# Revit family: SAL 50
name_source: partatom
category: Air Terminals
revit_build: Autodesk Revit 2017 (Build: 20160225_1515(x64)
units: mm (PartAtom-declared; Revit-internal decimal feet)

## family parameters
Always vertical = Yes
Cut with Voids When Loaded = No
Part Type = Normal
Room Calculation Point = No
Round Connector Dimension = Use Diameter
Shared = No
Work Plane-Based = No

## types (40) — shared parameters
Lw dB(A) = 30/35/40
Max Flow = 0.0 L/s
Maß A = 58.5 mm  [stored 0.191929 ft]
Maß C = 75 mm
Min Flow = 0.0 L/s
Product material = RAL 9016

## per-type parameters (varying)
- 600_1-reihig mit Anschlusskasten: Gewicht (g/m)=5607; Index=1; Index L=1; Index Reihig=1; L=600 mm; Maß B=101 mm  [stored 0.331365 ft]; Maß E=38.4 mm  [stored 0.125984 ft]; Maß F=48 mm  [stored 0.15748 ft]; Maß H=277 mm  [stored 0.908793 ft]; Maß K=51 mm; Maß M=75 mm; Maß Ø D=158 mm; Maß Ø D1=156 mm; Mindest-abstand (m)=8.3/>15.0/>15.0; Stutzen (Stk.)=1; Visible 1 Reihig=Yes; Visible 1 Stutzen=Yes; Visible 2 Reihig=No; Visible 2 Stutzen=No; Visible 3 Reihig=No; Visible 4 Reihig=No; x krit (m)=8.4/10.6/13.8; y (m)=1.6/2.1/2.6; Δp (Pa) 1=18/25/38; Δp (Pa) 2=21/31/42
- 750_1-reihig mit Anschlusskasten: Gewicht (g/m)=5607; Index=1; Index L=2; Index Reihig=1; L=750 mm  [stored 2.46063 ft]; Maß B=101 mm  [stored 0.331365 ft]; Maß E=38.4 mm  [stored 0.125984 ft]; Maß F=48 mm  [stored 0.15748 ft]; Maß H=277 mm  [stored 0.908793 ft]; Maß K=51 mm; Maß M=75 mm; Maß Ø D=158 mm; Maß Ø D1=156 mm; Mindest-abstand (m)=8.3/>15.0/>15.0; Stutzen (Stk.)=1; Visible 1 Reihig=Yes; Visible 1 Stutzen=Yes; Visible 2 Reihig=No; Visible 2 Stutzen=No; Visible 3 Reihig=No; Visible 4 Reihig=No; x krit (m)=8.4/10.6/13.8; y (m)=1.6/2.1/2.6; Δp (Pa) 1=18/25/38; Δp (Pa) 2=21/31/42
- 900_1-reihig mit Anschlusskasten: Gewicht (g/m)=5607; Index=1; Index L=3; Index Reihig=1; L=900 mm  [stored 2.95276 ft]; Maß B=101 mm  [stored 0.331365 ft]; Maß E=38.4 mm  [stored 0.125984 ft]; Maß F=48 mm  [stored 0.15748 ft]; Maß H=277 mm  [stored 0.908793 ft]; Maß K=51 mm; Maß M=75 mm; Maß Ø D=158 mm; Maß Ø D1=156 mm; Mindest-abstand (m)=8.3/>15.0/>15.0; Stutzen (Stk.)=1; Visible 1 Reihig=Yes; Visible 1 Stutzen=Yes; Visible 2 Reihig=No; Visible 2 Stutzen=No; Visible 3 Reihig=No; Visible 4 Reihig=No; x krit (m)=8.4/10.6/13.8; y (m)=1.6/2.1/2.6; Δp (Pa) 1=18/25/38; Δp (Pa) 2=21/31/42
- 1050_1-reihig mit Anschlusskasten: Gewicht (g/m)=5607; Index=1; Index L=4; Index Reihig=1; L=1050 mm; Maß B=101 mm  [stored 0.331365 ft]; Maß E=38.4 mm  [stored 0.125984 ft]; Maß F=48 mm  [stored 0.15748 ft]; Maß H=277 mm  [stored 0.908793 ft]; Maß K=51 mm; Maß M=75 mm; Maß Ø D=158 mm; Maß Ø D1=156 mm; Mindest-abstand (m)=8.3/>15.0/>15.0; Stutzen (Stk.)=1; Visible 1 Reihig=Yes; Visible 1 Stutzen=Yes; Visible 2 Reihig=No; Visible 2 Stutzen=No; Visible 3 Reihig=No; Visible 4 Reihig=No; x krit (m)=8.4/10.6/13.8; y (m)=1.6/2.1/2.6; Δp (Pa) 1=18/25/38; Δp (Pa) 2=21/31/42
- 1200_1-reihig mit Anschlusskasten: Gewicht (g/m)=5607; Index=1; Index L=5; Index Reihig=1; L=1200 mm; Maß B=101 mm  [stored 0.331365 ft]; Maß E=38.4 mm  [stored 0.125984 ft]; Maß F=48 mm  [stored 0.15748 ft]; Maß H=277 mm  [stored 0.908793 ft]; Maß K=51 mm; Maß M=75 mm; Maß Ø D=158 mm; Maß Ø D1=156 mm; Mindest-abstand (m)=8.3/>15.0/>15.0; Stutzen (Stk.)=1; Visible 1 Reihig=Yes; Visible 1 Stutzen=Yes; Visible 2 Reihig=No; Visible 2 Stutzen=No; Visible 3 Reihig=No; Visible 4 Reihig=No; x krit (m)=8.4/10.6/13.8; y (m)=1.6/2.1/2.6; Δp (Pa) 1=18/25/38; Δp (Pa) 2=21/31/42
- 1350_1-reihig mit Anschlusskasten: Gewicht (g/m)=5607; Index=1; Index L=6; Index Reihig=1; L=1350 mm  [stored 4.42913 ft]; Maß B=101 mm  [stored 0.331365 ft]; Maß E=38.4 mm  [stored 0.125984 ft]; Maß F=48 mm  [stored 0.15748 ft]; Maß H=277 mm  [stored 0.908793 ft]; Maß K=51 mm; Maß M=75 mm; Maß Ø D=158 mm; Maß Ø D1=156 mm; Mindest-abstand (m)=8.3/>15.0/>15.0; Stutzen (Stk.)=1; Visible 1 Reihig=Yes; Visible 1 Stutzen=Yes; Visible 2 Reihig=No; Visible 2 Stutzen=No; Visible 3 Reihig=No; Visible 4 Reihig=No; x krit (m)=8.4/10.6/13.8; y (m)=1.6/2.1/2.6; Δp (Pa) 1=18/25/38; Δp (Pa) 2=21/31/42
- 1500_1-reihig mit Anschlusskasten: Gewicht (g/m)=5607; Index=1; Index L=7; Index Reihig=1; L=1500 mm  [stored 4.92126 ft]; Maß B=101 mm  [stored 0.331365 ft]; Maß E=38.4 mm  [stored 0.125984 ft]; Maß F=48 mm  [stored 0.15748 ft]; Maß H=277 mm  [stored 0.908793 ft]; Maß K=51 mm; Maß M=75 mm; Maß Ø D=158 mm; Maß Ø D1=156 mm; Mindest-abstand (m)=8.3/>15.0/>15.0; Stutzen (Stk.)=1; Visible 1 Reihig=Yes; Visible 1 Stutzen=Yes; Visible 2 Reihig=No; Visible 2 Stutzen=No; Visible 3 Reihig=No; Visible 4 Reihig=No; x krit (m)=8.4/10.6/13.8; y (m)=1.6/2.1/2.6; Δp (Pa) 1=18/25/38; Δp (Pa) 2=21/31/42
- 1650_1-reihig mit Anschlusskasten: Gewicht (g/m)=5607; Index=2; Index L=8; Index Reihig=1; L=1650 mm; Maß B=101 mm  [stored 0.331365 ft]; Maß E=38.4 mm  [stored 0.125984 ft]; Maß F=48 mm  [stored 0.15748 ft]; Maß H=277 mm  [stored 0.908793 ft]; Maß K=51 mm; Maß M=75 mm; Maß Ø D=158 mm; Maß Ø D1=156 mm; Mindest-abstand (m)=8.3/>15.0/>15.0; Stutzen (Stk.)=2; Visible 1 Reihig=Yes; Visible 1 Stutzen=No; Visible 2 Reihig=No; Visible 2 Stutzen=Yes; Visible 3 Reihig=No; Visible 4 Reihig=No; x krit (m)=8.4/10.6/13.8; y (m)=1.6/2.1/2.6; Δp (Pa) 1=18/25/38; Δp (Pa) 2=21/31/42
- 1800_1-reihig mit Anschlusskasten: Gewicht (g/m)=5607; Index=2; Index L=9; Index Reihig=1; L=1800 mm; Maß B=101 mm  [stored 0.331365 ft]; Maß E=38.4 mm  [stored 0.125984 ft]; Maß F=48 mm  [stored 0.15748 ft]; Maß H=277 mm  [stored 0.908793 ft]; Maß K=51 mm; Maß M=75 mm; Maß Ø D=158 mm; Maß Ø D1=156 mm; Mindest-abstand (m)=8.3/>15.0/>15.0; Stutzen (Stk.)=2; Visible 1 Reihig=Yes; Visible 1 Stutzen=No; Visible 2 Reihig=No; Visible 2 Stutzen=Yes; Visible 3 Reihig=No; Visible 4 Reihig=No; x krit (m)=8.4/10.6/13.8; y (m)=1.6/2.1/2.6; Δp (Pa) 1=18/25/38; Δp (Pa) 2=21/31/42
- 1950_1-reihig mit Anschlusskasten: Gewicht (g/m)=5607; Index=2; Index L=10; Index Reihig=1; L=1950 mm; Maß B=101 mm  [stored 0.331365 ft]; Maß E=38.4 mm  [stored 0.125984 ft]; Maß F=48 mm  [stored 0.15748 ft]; Maß H=277 mm  [stored 0.908793 ft]; Maß K=51 mm; Maß M=75 mm; Maß Ø D=158 mm; Maß Ø D1=156 mm; Mindest-abstand (m)=8.3/>15.0/>15.0; Stutzen (Stk.)=2; Visible 1 Reihig=Yes; Visible 1 Stutzen=No; Visible 2 Reihig=No; Visible 2 Stutzen=Yes; Visible 3 Reihig=No; Visible 4 Reihig=No; x krit (m)=8.4/10.6/13.8; y (m)=1.6/2.1/2.6; Δp (Pa) 1=18/25/38; Δp (Pa) 2=21/31/42
- 600_2-reihig mit Anschlusskasten: Gewicht (g/m)=8293; Index=1; Index L=1; Index Reihig=2; L=600 mm; Maß B=148 mm  [stored 0.485564 ft]; Maß E=85 mm  [stored 0.278871 ft]; Maß F=94 mm  [stored 0.308399 ft]; Maß H=317 mm  [stored 1.04003 ft]; Maß K=97 mm  [stored 0.318241 ft]; Maß M=121 mm  [stored 0.396982 ft]; Maß Ø D=198 mm  [stored 0.649606 ft]; Maß Ø D1=196 mm  [stored 0.643045 ft]; Mindest-abstand (m)=15.0/>15.0/>15.0; Stutzen (Stk.)=1; Visible 1 Reihig=No; Visible 1 Stutzen=Yes; Visible 2 Reihig=Yes; Visible 2 Stutzen=No; Visible 3 Reihig=No; Visible 4 Reihig=No; x krit (m)=11.6/14.8/>15.0; y (m)=2.3/2.8/3.6; Δp (Pa) 1=15/22/30; Δp (Pa) 2=18/25/36
- 600_3-reihig mit Anschlusskasten: Gewicht (g/m)=10549; Index=1; Index L=1; Index Reihig=3; L=600 mm; Maß B=194 mm  [stored 0.636483 ft]; Maß E=131.6 mm  [stored 0.431759 ft]; Maß F=141 mm; Maß H=341 mm; Maß K=144 mm  [stored 0.472441 ft]; Maß M=168 mm  [stored 0.551181 ft]; Maß Ø D=222 mm; Maß Ø D1=220 mm  [stored 0.721785 ft]; Mindest-abstand (m)=15.0/>15.0/>15.0; Stutzen (Stk.)=1; Visible 1 Reihig=No; Visible 1 Stutzen=Yes; Visible 2 Reihig=No; Visible 2 Stutzen=No; Visible 3 Reihig=Yes; Visible 4 Reihig=No; x krit (m)=13.6/>15.0/>15.0; y (m)=2.7/3.4/4.3; Δp (Pa) 1=13/19/27; Δp (Pa) 2=16/22/31
- 600_4-reihig mit Anschlusskasten: Gewicht (g/m)=13135; Index=1; Index L=1; Index Reihig=4; L=600 mm; Maß B=241 mm  [stored 0.790682 ft]; Maß E=178.2 mm  [stored 0.584646 ft]; Maß F=187 mm  [stored 0.613517 ft]; Maß H=367 mm  [stored 1.20407 ft]; Maß K=190 mm; Maß M=215 mm; Maß Ø D=248 mm  [stored 0.813648 ft]; Maß Ø D1=246 mm  [stored 0.807087 ft]; Mindest-abstand (m)=15.0/>15.0/>15.0; Stutzen (Stk.)=1; Visible 1 Reihig=No; Visible 1 Stutzen=Yes; Visible 2 Reihig=No; Visible 2 Stutzen=No; Visible 3 Reihig=No; Visible 4 Reihig=Yes; x krit (m)=15.0/>15.0/>15.0; y (m)=3.0/3.8/4.7; Δp (Pa) 1=11/17/24; Δp (Pa) 2=14/20/28
- 750_2-reihig mit Anschlusskasten: Gewicht (g/m)=8293; Index=1; Index L=2; Index Reihig=2; L=750 mm  [stored 2.46063 ft]; Maß B=148 mm  [stored 0.485564 ft]; Maß E=85 mm  [stored 0.278871 ft]; Maß F=94 mm  [stored 0.308399 ft]; Maß H=317 mm  [stored 1.04003 ft]; Maß K=97 mm  [stored 0.318241 ft]; Maß M=121 mm  [stored 0.396982 ft]; Maß Ø D=198 mm  [stored 0.649606 ft]; Maß Ø D1=196 mm  [stored 0.643045 ft]; Mindest-abstand (m)=15.0/>15.0/>15.0; Stutzen (Stk.)=1; Visible 1 Reihig=No; Visible 1 Stutzen=Yes; Visible 2 Reihig=Yes; Visible 2 Stutzen=No; Visible 3 Reihig=No; Visible 4 Reihig=No; x krit (m)=11.6/14.8/>15.0; y (m)=2.3/2.8/3.6; Δp (Pa) 1=15/22/30; Δp (Pa) 2=18/25/36
- 750_3-reihig mit Anschlusskasten: Gewicht (g/m)=10549; Index=1; Index L=2; Index Reihig=3; L=750 mm  [stored 2.46063 ft]; Maß B=194 mm  [stored 0.636483 ft]; Maß E=131.6 mm  [stored 0.431759 ft]; Maß F=141 mm; Maß H=341 mm; Maß K=144 mm  [stored 0.472441 ft]; Maß M=168 mm  [stored 0.551181 ft]; Maß Ø D=222 mm; Maß Ø D1=220 mm  [stored 0.721785 ft]; Mindest-abstand (m)=15.0/>15.0/>15.0; Stutzen (Stk.)=1; Visible 1 Reihig=No; Visible 1 Stutzen=Yes; Visible 2 Reihig=No; Visible 2 Stutzen=No; Visible 3 Reihig=Yes; Visible 4 Reihig=No; x krit (m)=13.6/>15.0/>15.0; y (m)=2.7/3.4/4.3; Δp (Pa) 1=13/19/27; Δp (Pa) 2=16/22/31
- 750_4-reihig mit Anschlusskasten: Gewicht (g/m)=13135; Index=1; Index L=2; Index Reihig=4; L=750 mm  [stored 2.46063 ft]; Maß B=241 mm  [stored 0.790682 ft]; Maß E=178.2 mm  [stored 0.584646 ft]; Maß F=187 mm  [stored 0.613517 ft]; Maß H=367 mm  [stored 1.20407 ft]; Maß K=190 mm; Maß M=215 mm; Maß Ø D=248 mm  [stored 0.813648 ft]; Maß Ø D1=246 mm  [stored 0.807087 ft]; Mindest-abstand (m)=15.0/>15.0/>15.0; Stutzen (Stk.)=1; Visible 1 Reihig=No; Visible 1 Stutzen=Yes; Visible 2 Reihig=No; Visible 2 Stutzen=No; Visible 3 Reihig=No; Visible 4 Reihig=Yes; x krit (m)=15.0/>15.0/>15.0; y (m)=3.0/3.8/4.7; Δp (Pa) 1=11/17/24; Δp (Pa) 2=14/20/28
- 900_2-reihig mit Anschlusskasten: Gewicht (g/m)=8293; Index=1; Index L=3; Index Reihig=2; L=900 mm  [stored 2.95276 ft]; Maß B=148 mm  [stored 0.485564 ft]; Maß E=85 mm  [stored 0.278871 ft]; Maß F=94 mm  [stored 0.308399 ft]; Maß H=317 mm  [stored 1.04003 ft]; Maß K=97 mm  [stored 0.318241 ft]; Maß M=121 mm  [stored 0.396982 ft]; Maß Ø D=198 mm  [stored 0.649606 ft]; Maß Ø D1=196 mm  [stored 0.643045 ft]; Mindest-abstand (m)=15.0/>15.0/>15.0; Stutzen (Stk.)=1; Visible 1 Reihig=No; Visible 1 Stutzen=Yes; Visible 2 Reihig=Yes; Visible 2 Stutzen=No; Visible 3 Reihig=No; Visible 4 Reihig=No; x krit (m)=11.6/14.8/>15.0; y (m)=2.3/2.8/3.6; Δp (Pa) 1=15/22/30; Δp (Pa) 2=18/25/36
- 900_3-reihig mit Anschlusskasten: Gewicht (g/m)=10549; Index=1; Index L=3; Index Reihig=3; L=900 mm  [stored 2.95276 ft]; Maß B=194 mm  [stored 0.636483 ft]; Maß E=131.6 mm  [stored 0.431759 ft]; Maß F=141 mm; Maß H=341 mm; Maß K=144 mm  [stored 0.472441 ft]; Maß M=168 mm  [stored 0.551181 ft]; Maß Ø D=222 mm; Maß Ø D1=220 mm  [stored 0.721785 ft]; Mindest-abstand (m)=15.0/>15.0/>15.0; Stutzen (Stk.)=1; Visible 1 Reihig=No; Visible 1 Stutzen=Yes; Visible 2 Reihig=No; Visible 2 Stutzen=No; Visible 3 Reihig=Yes; Visible 4 Reihig=No; x krit (m)=13.6/>15.0/>15.0; y (m)=2.7/3.4/4.3; Δp (Pa) 1=13/19/27; Δp (Pa) 2=16/22/31
- 900_4-reihig mit Anschlusskasten: Gewicht (g/m)=13135; Index=1; Index L=3; Index Reihig=4; L=900 mm  [stored 2.95276 ft]; Maß B=241 mm  [stored 0.790682 ft]; Maß E=178.2 mm  [stored 0.584646 ft]; Maß F=187 mm  [stored 0.613517 ft]; Maß H=367 mm  [stored 1.20407 ft]; Maß K=190 mm; Maß M=215 mm; Maß Ø D=248 mm  [stored 0.813648 ft]; Maß Ø D1=246 mm  [stored 0.807087 ft]; Mindest-abstand (m)=15.0/>15.0/>15.0; Stutzen (Stk.)=1; Visible 1 Reihig=No; Visible 1 Stutzen=Yes; Visible 2 Reihig=No; Visible 2 Stutzen=No; Visible 3 Reihig=No; Visible 4 Reihig=Yes; x krit (m)=15.0/>15.0/>15.0; y (m)=3.0/3.8/4.7; Δp (Pa) 1=11/17/24; Δp (Pa) 2=14/20/28
- 1050_2-reihig mit Anschlusskasten: Gewicht (g/m)=8293; Index=1; Index L=4; Index Reihig=2; L=1050 mm; Maß B=148 mm  [stored 0.485564 ft]; Maß E=85 mm  [stored 0.278871 ft]; Maß F=94 mm  [stored 0.308399 ft]; Maß H=317 mm  [stored 1.04003 ft]; Maß K=97 mm  [stored 0.318241 ft]; Maß M=121 mm  [stored 0.396982 ft]; Maß Ø D=198 mm  [stored 0.649606 ft]; Maß Ø D1=196 mm  [stored 0.643045 ft]; Mindest-abstand (m)=15.0/>15.0/>15.0; Stutzen (Stk.)=1; Visible 1 Reihig=No; Visible 1 Stutzen=Yes; Visible 2 Reihig=Yes; Visible 2 Stutzen=No; Visible 3 Reihig=No; Visible 4 Reihig=No; x krit (m)=11.6/14.8/>15.0; y (m)=2.3/2.8/3.6; Δp (Pa) 1=15/22/30; Δp (Pa) 2=18/25/36
- 1050_3-reihig mit Anschlusskasten: Gewicht (g/m)=10549; Index=1; Index L=4; Index Reihig=3; L=1050 mm; Maß B=194 mm  [stored 0.636483 ft]; Maß E=131.6 mm  [stored 0.431759 ft]; Maß F=141 mm; Maß H=341 mm; Maß K=144 mm  [stored 0.472441 ft]; Maß M=168 mm  [stored 0.551181 ft]; Maß Ø D=222 mm; Maß Ø D1=220 mm  [stored 0.721785 ft]; Mindest-abstand (m)=15.0/>15.0/>15.0; Stutzen (Stk.)=1; Visible 1 Reihig=No; Visible 1 Stutzen=Yes; Visible 2 Reihig=No; Visible 2 Stutzen=No; Visible 3 Reihig=Yes; Visible 4 Reihig=No; x krit (m)=13.6/>15.0/>15.0; y (m)=2.7/3.4/4.3; Δp (Pa) 1=13/19/27; Δp (Pa) 2=16/22/31
- 1050_4-reihig mit Anschlusskasten: Gewicht (g/m)=13135; Index=1; Index L=4; Index Reihig=4; L=1050 mm; Maß B=241 mm  [stored 0.790682 ft]; Maß E=178.2 mm  [stored 0.584646 ft]; Maß F=187 mm  [stored 0.613517 ft]; Maß H=367 mm  [stored 1.20407 ft]; Maß K=190 mm; Maß M=215 mm; Maß Ø D=248 mm  [stored 0.813648 ft]; Maß Ø D1=246 mm  [stored 0.807087 ft]; Mindest-abstand (m)=15.0/>15.0/>15.0; Stutzen (Stk.)=1; Visible 1 Reihig=No; Visible 1 Stutzen=Yes; Visible 2 Reihig=No; Visible 2 Stutzen=No; Visible 3 Reihig=No; Visible 4 Reihig=Yes; x krit (m)=15.0/>15.0/>15.0; y (m)=3.0/3.8/4.7; Δp (Pa) 1=11/17/24; Δp (Pa) 2=14/20/28
- 1200_2-reihig mit Anschlusskasten: Gewicht (g/m)=8293; Index=1; Index L=5; Index Reihig=2; L=1200 mm; Maß B=148 mm  [stored 0.485564 ft]; Maß E=85 mm  [stored 0.278871 ft]; Maß F=94 mm  [stored 0.308399 ft]; Maß H=317 mm  [stored 1.04003 ft]; Maß K=97 mm  [stored 0.318241 ft]; Maß M=121 mm  [stored 0.396982 ft]; Maß Ø D=198 mm  [stored 0.649606 ft]; Maß Ø D1=196 mm  [stored 0.643045 ft]; Mindest-abstand (m)=15.0/>15.0/>15.0; Stutzen (Stk.)=1; Visible 1 Reihig=No; Visible 1 Stutzen=Yes; Visible 2 Reihig=Yes; Visible 2 Stutzen=No; Visible 3 Reihig=No; Visible 4 Reihig=No; x krit (m)=11.6/14.8/>15.0; y (m)=2.3/2.8/3.6; Δp (Pa) 1=15/22/30; Δp (Pa) 2=18/25/36
- 1200_3-reihig mit Anschlusskasten: Gewicht (g/m)=10549; Index=1; Index L=5; Index Reihig=3; L=1200 mm; Maß B=194 mm  [stored 0.636483 ft]; Maß E=131.6 mm  [stored 0.431759 ft]; Maß F=141 mm; Maß H=341 mm; Maß K=144 mm  [stored 0.472441 ft]; Maß M=168 mm  [stored 0.551181 ft]; Maß Ø D=222 mm; Maß Ø D1=220 mm  [stored 0.721785 ft]; Mindest-abstand (m)=15.0/>15.0/>15.0; Stutzen (Stk.)=1; Visible 1 Reihig=No; Visible 1 Stutzen=Yes; Visible 2 Reihig=No; Visible 2 Stutzen=No; Visible 3 Reihig=Yes; Visible 4 Reihig=No; x krit (m)=13.6/>15.0/>15.0; y (m)=2.7/3.4/4.3; Δp (Pa) 1=13/19/27; Δp (Pa) 2=16/22/31
- 1200_4-reihig mit Anschlusskasten: Gewicht (g/m)=13135; Index=1; Index L=5; Index Reihig=4; L=1200 mm; Maß B=241 mm  [stored 0.790682 ft]; Maß E=178.2 mm  [stored 0.584646 ft]; Maß F=187 mm  [stored 0.613517 ft]; Maß H=367 mm  [stored 1.20407 ft]; Maß K=190 mm; Maß M=215 mm; Maß Ø D=248 mm  [stored 0.813648 ft]; Maß Ø D1=246 mm  [stored 0.807087 ft]; Mindest-abstand (m)=15.0/>15.0/>15.0; Stutzen (Stk.)=1; Visible 1 Reihig=No; Visible 1 Stutzen=Yes; Visible 2 Reihig=No; Visible 2 Stutzen=No; Visible 3 Reihig=No; Visible 4 Reihig=Yes; x krit (m)=15.0/>15.0/>15.0; y (m)=3.0/3.8/4.7; Δp (Pa) 1=11/17/24; Δp (Pa) 2=14/20/28
- 1350_2-reihig mit Anschlusskasten: Gewicht (g/m)=8293; Index=1; Index L=6; Index Reihig=2; L=1350 mm  [stored 4.42913 ft]; Maß B=148 mm  [stored 0.485564 ft]; Maß E=85 mm  [stored 0.278871 ft]; Maß F=94 mm  [stored 0.308399 ft]; Maß H=317 mm  [stored 1.04003 ft]; Maß K=97 mm  [stored 0.318241 ft]; Maß M=121 mm  [stored 0.396982 ft]; Maß Ø D=198 mm  [stored 0.649606 ft]; Maß Ø D1=196 mm  [stored 0.643045 ft]; Mindest-abstand (m)=15.0/>15.0/>15.0; Stutzen (Stk.)=1; Visible 1 Reihig=No; Visible 1 Stutzen=Yes; Visible 2 Reihig=Yes; Visible 2 Stutzen=No; Visible 3 Reihig=No; Visible 4 Reihig=No; x krit (m)=11.6/14.8/>15.0; y (m)=2.3/2.8/3.6; Δp (Pa) 1=15/22/30; Δp (Pa) 2=18/25/36
- 1350_3-reihig mit Anschlusskasten: Gewicht (g/m)=10549; Index=1; Index L=6; Index Reihig=3; L=1350 mm  [stored 4.42913 ft]; Maß B=194 mm  [stored 0.636483 ft]; Maß E=131.6 mm  [stored 0.431759 ft]; Maß F=141 mm; Maß H=341 mm; Maß K=144 mm  [stored 0.472441 ft]; Maß M=168 mm  [stored 0.551181 ft]; Maß Ø D=222 mm; Maß Ø D1=220 mm  [stored 0.721785 ft]; Mindest-abstand (m)=15.0/>15.0/>15.0; Stutzen (Stk.)=1; Visible 1 Reihig=No; Visible 1 Stutzen=Yes; Visible 2 Reihig=No; Visible 2 Stutzen=No; Visible 3 Reihig=Yes; Visible 4 Reihig=No; x krit (m)=13.6/>15.0/>15.0; y (m)=2.7/3.4/4.3; Δp (Pa) 1=13/19/27; Δp (Pa) 2=16/22/31
- 1350_4-reihig mit Anschlusskasten: Gewicht (g/m)=13135; Index=1; Index L=6; Index Reihig=4; L=1350 mm  [stored 4.42913 ft]; Maß B=241 mm  [stored 0.790682 ft]; Maß E=178.2 mm  [stored 0.584646 ft]; Maß F=187 mm  [stored 0.613517 ft]; Maß H=367 mm  [stored 1.20407 ft]; Maß K=190 mm; Maß M=215 mm; Maß Ø D=248 mm  [stored 0.813648 ft]; Maß Ø D1=246 mm  [stored 0.807087 ft]; Mindest-abstand (m)=15.0/>15.0/>15.0; Stutzen (Stk.)=1; Visible 1 Reihig=No; Visible 1 Stutzen=Yes; Visible 2 Reihig=No; Visible 2 Stutzen=No; Visible 3 Reihig=No; Visible 4 Reihig=Yes; x krit (m)=15.0/>15.0/>15.0; y (m)=3.0/3.8/4.7; Δp (Pa) 1=11/17/24; Δp (Pa) 2=14/20/28
- 1500_2-reihig mit Anschlusskasten: Gewicht (g/m)=8293; Index=1; Index L=7; Index Reihig=2; L=1500 mm  [stored 4.92126 ft]; Maß B=148 mm  [stored 0.485564 ft]; Maß E=85 mm  [stored 0.278871 ft]; Maß F=94 mm  [stored 0.308399 ft]; Maß H=317 mm  [stored 1.04003 ft]; Maß K=97 mm  [stored 0.318241 ft]; Maß M=121 mm  [stored 0.396982 ft]; Maß Ø D=198 mm  [stored 0.649606 ft]; Maß Ø D1=196 mm  [stored 0.643045 ft]; Mindest-abstand (m)=15.0/>15.0/>15.0; Stutzen (Stk.)=1; Visible 1 Reihig=No; Visible 1 Stutzen=Yes; Visible 2 Reihig=Yes; Visible 2 Stutzen=No; Visible 3 Reihig=No; Visible 4 Reihig=No; x krit (m)=11.6/14.8/>15.0; y (m)=2.3/2.8/3.6; Δp (Pa) 1=15/22/30; Δp (Pa) 2=18/25/36
- 1500_3-reihig mit Anschlusskasten: Gewicht (g/m)=10549; Index=1; Index L=7; Index Reihig=3; L=1500 mm  [stored 4.92126 ft]; Maß B=194 mm  [stored 0.636483 ft]; Maß E=131.6 mm  [stored 0.431759 ft]; Maß F=141 mm; Maß H=341 mm; Maß K=144 mm  [stored 0.472441 ft]; Maß M=168 mm  [stored 0.551181 ft]; Maß Ø D=222 mm; Maß Ø D1=220 mm  [stored 0.721785 ft]; Mindest-abstand (m)=15.0/>15.0/>15.0; Stutzen (Stk.)=1; Visible 1 Reihig=No; Visible 1 Stutzen=Yes; Visible 2 Reihig=No; Visible 2 Stutzen=No; Visible 3 Reihig=Yes; Visible 4 Reihig=No; x krit (m)=13.6/>15.0/>15.0; y (m)=2.7/3.4/4.3; Δp (Pa) 1=13/19/27; Δp (Pa) 2=16/22/31
- 1500_4-reihig mit Anschlusskasten: Gewicht (g/m)=13135; Index=1; Index L=7; Index Reihig=4; L=1500 mm  [stored 4.92126 ft]; Maß B=241 mm  [stored 0.790682 ft]; Maß E=178.2 mm  [stored 0.584646 ft]; Maß F=187 mm  [stored 0.613517 ft]; Maß H=367 mm  [stored 1.20407 ft]; Maß K=190 mm; Maß M=215 mm; Maß Ø D=248 mm  [stored 0.813648 ft]; Maß Ø D1=246 mm  [stored 0.807087 ft]; Mindest-abstand (m)=15.0/>15.0/>15.0; Stutzen (Stk.)=1; Visible 1 Reihig=No; Visible 1 Stutzen=Yes; Visible 2 Reihig=No; Visible 2 Stutzen=No; Visible 3 Reihig=No; Visible 4 Reihig=Yes; x krit (m)=15.0/>15.0/>15.0; y (m)=3.0/3.8/4.7; Δp (Pa) 1=11/17/24; Δp (Pa) 2=14/20/28
- 1650_2-reihig mit Anschlusskasten: Gewicht (g/m)=8293; Index=2; Index L=8; Index Reihig=2; L=1650 mm; Maß B=148 mm  [stored 0.485564 ft]; Maß E=85 mm  [stored 0.278871 ft]; Maß F=94 mm  [stored 0.308399 ft]; Maß H=317 mm  [stored 1.04003 ft]; Maß K=97 mm  [stored 0.318241 ft]; Maß M=121 mm  [stored 0.396982 ft]; Maß Ø D=198 mm  [stored 0.649606 ft]; Maß Ø D1=196 mm  [stored 0.643045 ft]; Mindest-abstand (m)=15.0/>15.0/>15.0; Stutzen (Stk.)=2; Visible 1 Reihig=No; Visible 1 Stutzen=No; Visible 2 Reihig=Yes; Visible 2 Stutzen=Yes; Visible 3 Reihig=No; Visible 4 Reihig=No; x krit (m)=11.6/14.8/>15.0; y (m)=2.3/2.8/3.6; Δp (Pa) 1=15/22/30; Δp (Pa) 2=18/25/36
- 1650_3-reihig mit Anschlusskasten: Gewicht (g/m)=10549; Index=2; Index L=8; Index Reihig=3; L=1650 mm; Maß B=194 mm  [stored 0.636483 ft]; Maß E=131.6 mm  [stored 0.431759 ft]; Maß F=141 mm; Maß H=341 mm; Maß K=144 mm  [stored 0.472441 ft]; Maß M=168 mm  [stored 0.551181 ft]; Maß Ø D=222 mm; Maß Ø D1=220 mm  [stored 0.721785 ft]; Mindest-abstand (m)=15.0/>15.0/>15.0; Stutzen (Stk.)=2; Visible 1 Reihig=No; Visible 1 Stutzen=No; Visible 2 Reihig=No; Visible 2 Stutzen=Yes; Visible 3 Reihig=Yes; Visible 4 Reihig=No; x krit (m)=13.6/>15.0/>15.0; y (m)=2.7/3.4/4.3; Δp (Pa) 1=13/19/27; Δp (Pa) 2=16/22/31
- 1650_4-reihig mit Anschlusskasten: Gewicht (g/m)=13135; Index=2; Index L=8; Index Reihig=4; L=1650 mm; Maß B=241 mm  [stored 0.790682 ft]; Maß E=178.2 mm  [stored 0.584646 ft]; Maß F=187 mm  [stored 0.613517 ft]; Maß H=367 mm  [stored 1.20407 ft]; Maß K=190 mm; Maß M=215 mm; Maß Ø D=248 mm  [stored 0.813648 ft]; Maß Ø D1=246 mm  [stored 0.807087 ft]; Mindest-abstand (m)=15.0/>15.0/>15.0; Stutzen (Stk.)=2; Visible 1 Reihig=No; Visible 1 Stutzen=No; Visible 2 Reihig=No; Visible 2 Stutzen=Yes; Visible 3 Reihig=No; Visible 4 Reihig=Yes; x krit (m)=15.0/>15.0/>15.0; y (m)=3.0/3.8/4.7; Δp (Pa) 1=11/17/24; Δp (Pa) 2=14/20/28
- 1800_2-reihig mit Anschlusskasten: Gewicht (g/m)=8293; Index=2; Index L=9; Index Reihig=2; L=1800 mm; Maß B=148 mm  [stored 0.485564 ft]; Maß E=85 mm  [stored 0.278871 ft]; Maß F=94 mm  [stored 0.308399 ft]; Maß H=317 mm  [stored 1.04003 ft]; Maß K=97 mm  [stored 0.318241 ft]; Maß M=121 mm  [stored 0.396982 ft]; Maß Ø D=198 mm  [stored 0.649606 ft]; Maß Ø D1=196 mm  [stored 0.643045 ft]; Mindest-abstand (m)=15.0/>15.0/>15.0; Stutzen (Stk.)=2; Visible 1 Reihig=No; Visible 1 Stutzen=No; Visible 2 Reihig=Yes; Visible 2 Stutzen=Yes; Visible 3 Reihig=No; Visible 4 Reihig=No; x krit (m)=11.6/14.8/>15.0; y (m)=2.3/2.8/3.6; Δp (Pa) 1=15/22/30; Δp (Pa) 2=18/25/36
- 1800_3-reihig mit Anschlusskasten: Gewicht (g/m)=10549; Index=2; Index L=9; Index Reihig=3; L=1800 mm; Maß B=194 mm  [stored 0.636483 ft]; Maß E=131.6 mm  [stored 0.431759 ft]; Maß F=141 mm; Maß H=341 mm; Maß K=144 mm  [stored 0.472441 ft]; Maß M=168 mm  [stored 0.551181 ft]; Maß Ø D=222 mm; Maß Ø D1=220 mm  [stored 0.721785 ft]; Mindest-abstand (m)=15.0/>15.0/>15.0; Stutzen (Stk.)=2; Visible 1 Reihig=No; Visible 1 Stutzen=No; Visible 2 Reihig=No; Visible 2 Stutzen=Yes; Visible 3 Reihig=Yes; Visible 4 Reihig=No; x krit (m)=13.6/>15.0/>15.0; y (m)=2.7/3.4/4.3; Δp (Pa) 1=13/19/27; Δp (Pa) 2=16/22/31
- 1800_4-reihig mit Anschlusskasten: Gewicht (g/m)=13135; Index=2; Index L=9; Index Reihig=4; L=1800 mm; Maß B=241 mm  [stored 0.790682 ft]; Maß E=178.2 mm  [stored 0.584646 ft]; Maß F=187 mm  [stored 0.613517 ft]; Maß H=367 mm  [stored 1.20407 ft]; Maß K=190 mm; Maß M=215 mm; Maß Ø D=248 mm  [stored 0.813648 ft]; Maß Ø D1=246 mm  [stored 0.807087 ft]; Mindest-abstand (m)=15.0/>15.0/>15.0; Stutzen (Stk.)=2; Visible 1 Reihig=No; Visible 1 Stutzen=No; Visible 2 Reihig=No; Visible 2 Stutzen=Yes; Visible 3 Reihig=No; Visible 4 Reihig=Yes; x krit (m)=15.0/>15.0/>15.0; y (m)=3.0/3.8/4.7; Δp (Pa) 1=11/17/24; Δp (Pa) 2=14/20/28
- 1950_2-reihig mit Anschlusskasten: Gewicht (g/m)=8293; Index=2; Index L=10; Index Reihig=2; L=1950 mm; Maß B=148 mm  [stored 0.485564 ft]; Maß E=85 mm  [stored 0.278871 ft]; Maß F=94 mm  [stored 0.308399 ft]; Maß H=317 mm  [stored 1.04003 ft]; Maß K=97 mm  [stored 0.318241 ft]; Maß M=121 mm  [stored 0.396982 ft]; Maß Ø D=198 mm  [stored 0.649606 ft]; Maß Ø D1=196 mm  [stored 0.643045 ft]; Mindest-abstand (m)=15.0/>15.0/>15.0; Stutzen (Stk.)=2; Visible 1 Reihig=Yes; Visible 1 Stutzen=No; Visible 2 Reihig=No; Visible 2 Stutzen=Yes; Visible 3 Reihig=No; Visible 4 Reihig=No; x krit (m)=11.6/14.8/>15.0; y (m)=2.3/2.8/3.6; Δp (Pa) 1=15/22/30; Δp (Pa) 2=18/25/36
- 1950_3-reihig mit Anschlusskasten: Gewicht (g/m)=10549; Index=2; Index L=10; Index Reihig=3; L=1950 mm; Maß B=194 mm  [stored 0.636483 ft]; Maß E=131.6 mm  [stored 0.431759 ft]; Maß F=141 mm; Maß H=341 mm; Maß K=144 mm  [stored 0.472441 ft]; Maß M=168 mm  [stored 0.551181 ft]; Maß Ø D=222 mm; Maß Ø D1=220 mm  [stored 0.721785 ft]; Mindest-abstand (m)=15.0/>15.0/>15.0; Stutzen (Stk.)=2; Visible 1 Reihig=No; Visible 1 Stutzen=No; Visible 2 Reihig=No; Visible 2 Stutzen=Yes; Visible 3 Reihig=Yes; Visible 4 Reihig=No; x krit (m)=13.6/>15.0/>15.0; y (m)=2.7/3.4/4.3; Δp (Pa) 1=13/19/27; Δp (Pa) 2=16/22/31
- 1950_4-reihig mit Anschlusskasten: Gewicht (g/m)=13135; Index=2; Index L=10; Index Reihig=4; L=1950 mm; Maß B=241 mm  [stored 0.790682 ft]; Maß E=178.2 mm  [stored 0.584646 ft]; Maß F=187 mm  [stored 0.613517 ft]; Maß H=367 mm  [stored 1.20407 ft]; Maß K=190 mm; Maß M=215 mm; Maß Ø D=248 mm  [stored 0.813648 ft]; Maß Ø D1=246 mm  [stored 0.807087 ft]; Mindest-abstand (m)=15.0/>15.0/>15.0; Stutzen (Stk.)=2; Visible 1 Reihig=No; Visible 1 Stutzen=No; Visible 2 Reihig=No; Visible 2 Stutzen=Yes; Visible 3 Reihig=No; Visible 4 Reihig=Yes; x krit (m)=15.0/>15.0/>15.0; y (m)=3.0/3.8/4.7; Δp (Pa) 1=11/17/24; Δp (Pa) 2=14/20/28

note: [stored X ft] marks values corroborated as IEEE doubles in the binary element streams (Revit-internal decimal feet)

## geometry (parser evidence)
native form markers: Sweep x14
no freeform markers — native parametric forms only
